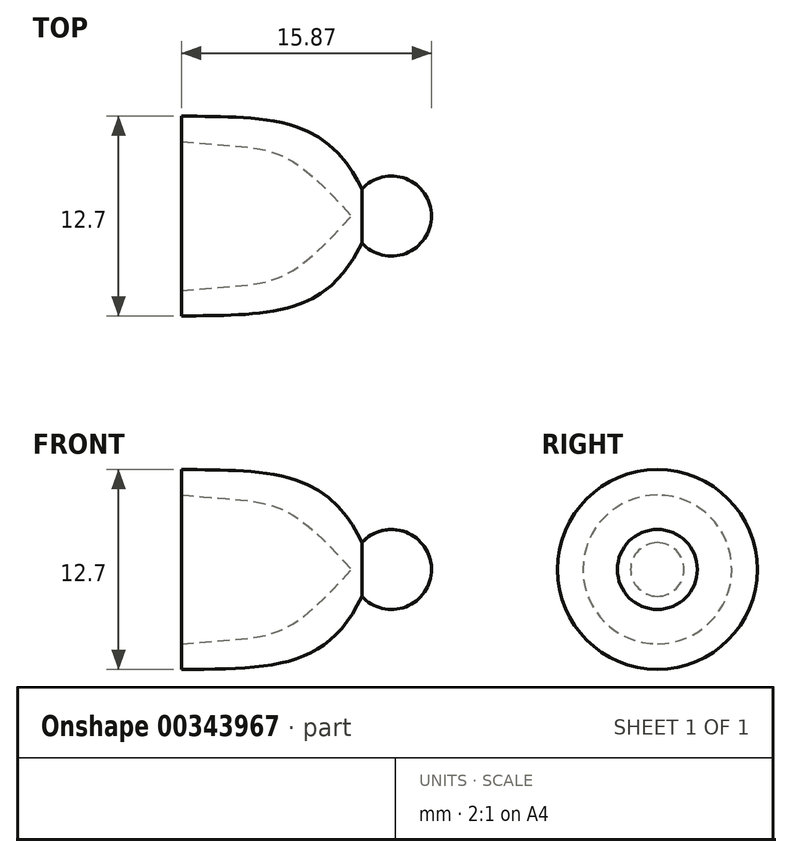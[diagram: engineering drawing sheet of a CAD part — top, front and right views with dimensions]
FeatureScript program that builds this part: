
annotation { "Feature Type Name" : "Feature", "Feature Type Description" : "" }
export const myFeature = defineFeature(function(context is Context, id is Id, definition is map)
    precondition{}
    {
        {
            var Q0;
            Q0=qCreatedBy(makeId("Front.planeOp"),FACE);
            var sketch = newSketch(context, id + "F0", { "sketchPlane" : qUnion([Q0])});
            skLineSegment(sketch, "E0", {"start": v(0, 0) * mm, "end": v(-15.87, 0) * mm});
            skLineSegment(sketch, "E1", {"start": v(-15.87, 0) * mm, "end": v(-15.87, 6.35) * mm});
            skCircle(sketch, "E2", {"center": v(-2.54, 0) * mm, "radius": 2.54 * mm});
            skFitSpline(sketch, "E3", {"points": [v(-15.87, 6.35) * mm, v(-4.42, 1.7) * mm], "startDerivative": vector(17.03, -0.22) * mm, "endDerivative": vector(6.55, -14.05) * mm});
            skFitSpline(sketch, "E4", {"points": [v(-15.87, 4.73) * mm, v(-12.69, 4.47) * mm, v(-9.23, 3.7) * mm, v(-5.08, 0) * mm], "startDerivative": vector(10.62, -0.85) * mm, "endDerivative": vector(10.44, -11.38) * mm});
            skSolve(sketch);
        }
        {
            var Q0;
            {var subQ0=sQuery(id+"F0.wireOp",EDGE,"E3");Q0=makeQuery(id+"F0.imprint","IMPRINT",FACE,{"disambiguationData":[TD([[makeQuery(id+"F0.imprint","IMPRINT",EDGE,{"derivedFrom":subQ0}),-1.0]])]});}
            var Q1;
            {var subQ0=sQuery(id+"F0.wireOp",EDGE,"E2");var subQ1=sQuery(id+"F0.wireOp",EDGE,"E0");var subQ2=makeQuery(id+"F0.imprint","INTERSECT",VERTEX,{"derivedFrom":[subQ1,subQ0]});Q1=makeQuery(id+"F0.imprint","IMPRINT",FACE,{"disambiguationData":[TD([[makeQuery(id+"F0.imprint","IMPRINT",EDGE,{"disambiguationData":[TD([[subQ2,-1.0]])],"derivedFrom":subQ0}),1.0]])]});}
            var Q2;
            Q2=sQuery(id+"F0.wireOp",EDGE,"E0");
            revolve(context, id + "F1", {"entities" : qUnion([Q0, Q1]), "axis" : qUnion([Q2]), "revolveType" : RevolveType.FULL});
        }
    });
